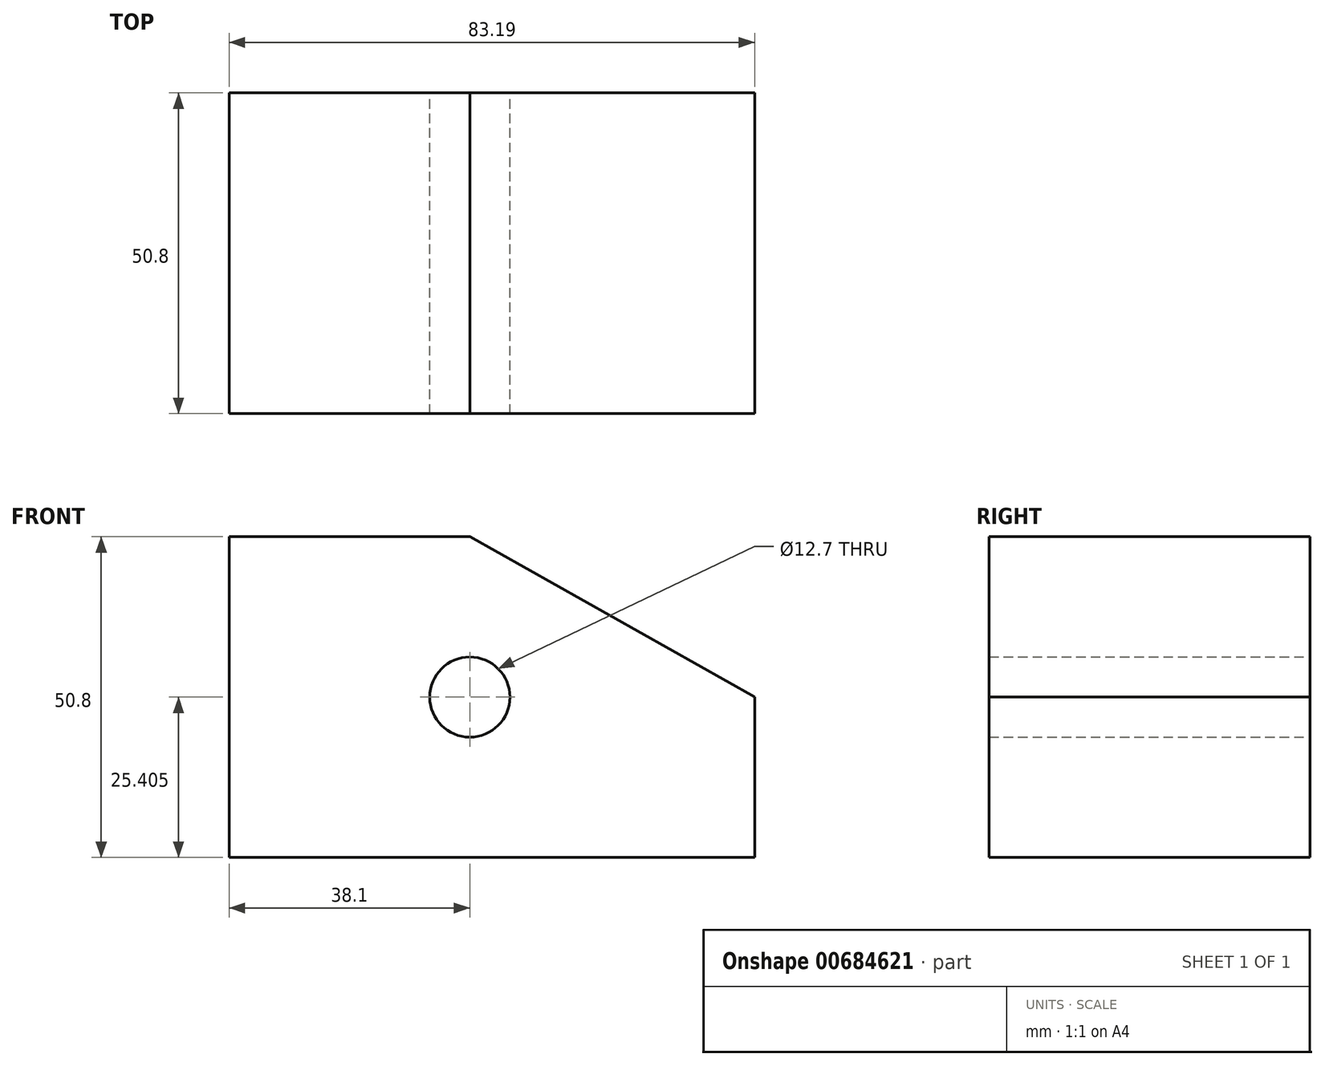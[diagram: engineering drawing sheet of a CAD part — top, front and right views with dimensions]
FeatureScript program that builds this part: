
annotation { "Feature Type Name" : "Feature", "Feature Type Description" : "" }
export const myFeature = defineFeature(function(context is Context, id is Id, definition is map)
    precondition{}
    {
        {
            var Q0;
            Q0=qCreatedBy(makeId("Front.planeOp"),FACE);
            var sketch = newSketch(context, id + "F0", { "sketchPlane" : qUnion([Q0])});
            skLineSegment(sketch, "E0", {"start": v(-57.2, 19.34) * mm, "end": v(-57.2, -31.46) * mm});
            skLineSegment(sketch, "E1", {"start": v(-57.2, 19.34) * mm, "end": v(-19.1, 19.34) * mm});
            skLineSegment(sketch, "E2", {"start": v(-57.2, -31.46) * mm, "end": v(26, -31.46) * mm});
            skLineSegment(sketch, "E3", {"start": v(26, -31.46) * mm, "end": v(26, -6.06) * mm});
            skLineSegment(sketch, "E4", {"start": v(-19.1, 19.34) * mm, "end": v(26, -6.06) * mm});
            skPoint(sketch, "E5", {"position": v(-19.1, -6.06) * mm});
            skCircle(sketch, "E6", {"center": v(-19.1, -6.06) * mm, "radius": 6.35 * mm});
            skSolve(sketch);
        }
        {
            var Q0;
            Q0=makeQuery(id+"F0.imprint","IMPRINT",FACE,{"disambiguationData":[TD([[makeQuery(id+"F0.imprint","IMPRINT",EDGE,{"derivedFrom":sQuery(id+"F0.wireOp",EDGE,"E0")}),1.0]])]});
            extrude(context, id + "F1", {"entities" : qUnion([Q0]), "depth" : 50.8 * mm, "offsetDistance" : 25.4 * mm});
        }
    });
